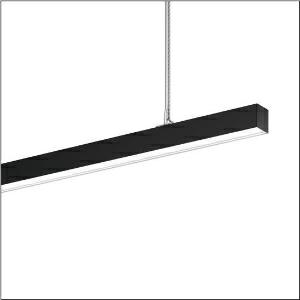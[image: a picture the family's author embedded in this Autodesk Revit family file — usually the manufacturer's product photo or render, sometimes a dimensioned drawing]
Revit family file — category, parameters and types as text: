
# Revit family: silica_r__21_51mx30dc49bb_d1ca
name_source: partatom
category: Lighting Fixtures
units: mm (PartAtom-declared; Revit-internal decimal feet)

## family parameters
Cut with Voids When Loaded = No
Host = Face
Light Source = No
Part Type = Normal
Room Calculation Point = No
Round Connector Dimension = Use Diameter
Shared = No

## types (1)
- --- (1 x LED, 10520 lm, 64.1 W, 4000K)
    Apparent Load = 64 VA
    CIE Flux Codes = 47 79 96 57 100
    Color Rendering = 80
    Color Temperature = 4000K
    Default Elevation = 1800 mm
    Description = Silica® 21, office luminaire, primary optical cover: cover, of PMMA, opal, light emission: direct/indirect distribution, primary light characteristic: symmetric, installation type: suspended mounting, LED, rated luminous flux: 10.520lm, luminous efficacy: 164lm/W, light colour: 840, colour temperature: 4000K, with terminal, 3+2-pole, max. 2.5mm², mains connection: 220..240V, AC, 50/60Hz, rated input power: 64.1W, luminaire housing, of aluminium, jet black (RAL 9005), length: 3.004mm, width: 53mm, height: 53mm, protection rating (complete): IP20, insulation class (complete): insulation class I (protective earthing), certification: CE, permissible operating ambient temperature: 0..+35°C, standard: EN 50419, packaging unit: 1 piece
    Height = 53 mm
    Lamp = 1 x LED
    Lamp Light Flux = 10520 lm
    Lamp Power = 64.1 W
    Lamp count = 1
    Length = 3004 mm
    Luminous efficacy = 164 lm/W
    Manufacturer = Siteco
    ModVariant = No
    Model = 51MX30DC49BB
    Mounting Place = Ceiling
    Mounting Type = Pendant
    Number of Poles = 1
    OnlyDefault = Yes
    Power Factor = 1
    Product Name = Silica® 21
    Product group = office luminaire | ceiling pendant
    ProductGroupID = 902
    Protection Class = Protection class I
    Protection Degree = IP 20
    RLX_Detail_Level = 1
    RLX_Emergency_Light_Flux = 0 lm
    RLX_Emergency_Type = 0
    RLX_Emergency_Type_DB = No
    RlxData = <blob elided: 26085 chars, md5=55722812>
    Socket = socket
    Standby Power = 0 W
    System Light Flux = 10520 lm
    System Power = 64 W
    Type Comments = factory setting: luminous flux: 100 % | dim-lin: 254 | 218 mA
    Type Image = l_1335856.jpg
    URL = http://relux.com
    VarID = @adj_086115
    Voltage = 0 V
    Weight = 0.00 kg
    Width = 53 mm

## geometry (parser evidence)
native form markers: Blend x4, Sweep x10
no freeform markers — native parametric forms only
